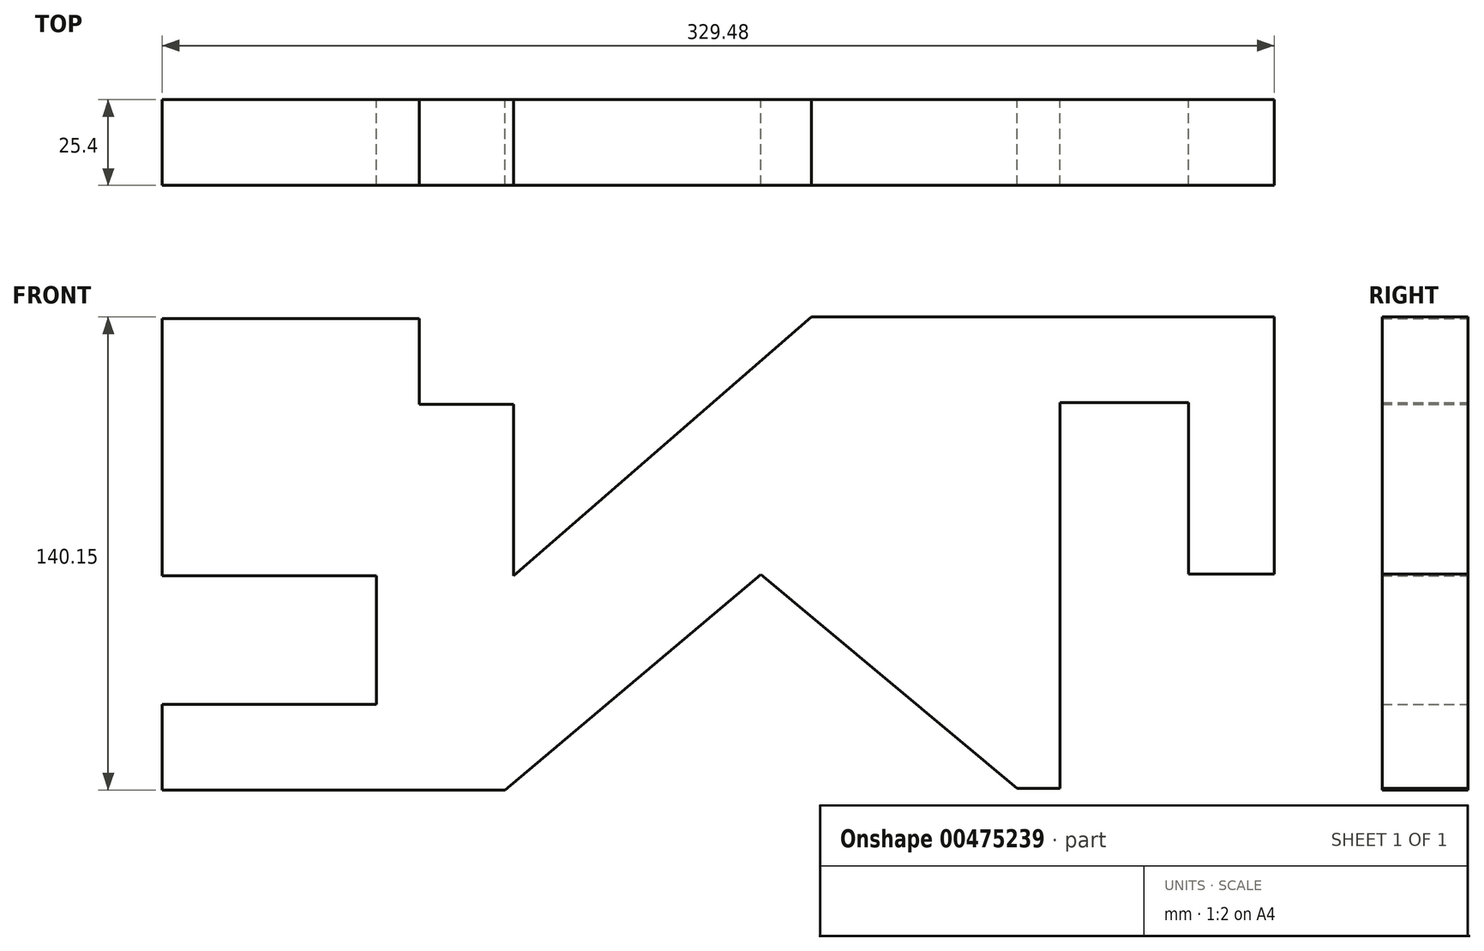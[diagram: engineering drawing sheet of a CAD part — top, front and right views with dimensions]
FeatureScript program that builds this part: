
annotation { "Feature Type Name" : "Feature", "Feature Type Description" : "" }
export const myFeature = defineFeature(function(context is Context, id is Id, definition is map)
    precondition{}
    {
        {
            var Q0;
            Q0=qCreatedBy(makeId("Front.planeOp"),FACE);
            var sketch = newSketch(context, id + "F0", { "sketchPlane" : qUnion([Q0])});
            skLineSegment(sketch, "E0", {"start": v(0, 0) * mm, "end": v(0, -76.2) * mm});
            skLineSegment(sketch, "E1", {"start": v(0, -76.2) * mm, "end": v(63.5, -76.2) * mm});
            skLineSegment(sketch, "E2", {"start": v(63.5, -76.2) * mm, "end": v(63.5, -114.3) * mm});
            skLineSegment(sketch, "E3", {"start": v(63.5, -114.3) * mm, "end": v(0, -114.3) * mm});
            skLineSegment(sketch, "E4", {"start": v(0, -114.3) * mm, "end": v(0, -139.7) * mm});
            skLineSegment(sketch, "E5", {"start": v(0, -139.7) * mm, "end": v(101.6, -139.7) * mm});
            skLineSegment(sketch, "E6", {"start": v(0, 0) * mm, "end": v(76.2, 0) * mm});
            skLineSegment(sketch, "E7", {"start": v(76.2, 0) * mm, "end": v(76.2, -25.4) * mm});
            skLineSegment(sketch, "E8", {"start": v(76.2, -25.4) * mm, "end": v(104.14, -25.4) * mm});
            skLineSegment(sketch, "E9", {"start": v(104.14, -25.4) * mm, "end": v(104.14, -76.2) * mm});
            skLineSegment(sketch, "E10", {"start": v(104.14, -76.2) * mm, "end": v(192.32, 0.45) * mm});
            skLineSegment(sketch, "E11", {"start": v(192.32, 0.45) * mm, "end": v(329.48, 0.45) * mm});
            skLineSegment(sketch, "E12", {"start": v(329.48, 0.45) * mm, "end": v(329.48, -75.75) * mm});
            skLineSegment(sketch, "E13", {"start": v(329.48, -75.75) * mm, "end": v(304.08, -75.75) * mm});
            skLineSegment(sketch, "E14", {"start": v(304.08, -75.75) * mm, "end": v(304.08, -24.95) * mm});
            skLineSegment(sketch, "E15", {"start": v(304.08, -24.95) * mm, "end": v(265.98, -24.95) * mm});
            skLineSegment(sketch, "E16", {"start": v(265.98, -24.95) * mm, "end": v(265.98, -139.25) * mm});
            skLineSegment(sketch, "E17", {"start": v(265.98, -139.25) * mm, "end": v(253.28, -139.25) * mm});
            skLineSegment(sketch, "E18", {"start": v(101.6, -139.7) * mm, "end": v(177.44, -75.75) * mm});
            skLineSegment(sketch, "E19", {"start": v(177.28, -75.8) * mm, "end": v(253.28, -139.25) * mm});
            skSolve(sketch);
        }
        {
            var Q0;
            Q0=makeQuery(id+"F0.imprint","IMPRINT",FACE,{"disambiguationData":[TD([[makeQuery(id+"F0.imprint","IMPRINT",EDGE,{"derivedFrom":sQuery(id+"F0.wireOp",EDGE,"E0")}),1.0]])]});
            extrude(context, id + "F1", {"entities" : qUnion([Q0]), "depth" : 25.4 * mm});
        }
    });
